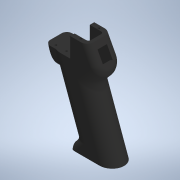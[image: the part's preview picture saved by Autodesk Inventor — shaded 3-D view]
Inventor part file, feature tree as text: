
AUTODESK INVENTOR PART (.ipt)
format: ipt  version: 2021 (Build 250183000, 183)  size: 737,280 bytes
history: native  units: mm
features: extrude x12, sketch x12, fillet x10, projected_geometry x5, plane x1, chamfer x1
ambient origin geometry x8: Origin, YZ Plane, XZ Plane, XY Plane, X Axis, Y Axis, Z Axis, Center Point
bodies: Solid1 (feature_tree)
feature tree (41):
  extrude  "Extrusion1"  TaperAngle=120.0deg  [1 undecoded]
  fillet  "Fillet10"  Radius=6.0mm
  fillet  "Fillet12"  Radius=45.0mm
  fillet  "Fillet13"  Radius=3.490659mm
  fillet  "Fillet11"  Radius=5.0mm
  extrude  "Extrusion29"  Depth=30.0mm
  extrude  "Extrusion30"  Depth=8.5mm
  plane  "Work Plane2"
  extrude  "Extrusion40"  Depth=20.0mm
  extrude  "Extrusion41"  Depth=33.0mm TaperAngle=0.0deg
  extrude  "Extrusion32"  Depth=12.0mm
  extrude  "Extrusion39"  Depth=10.0mm
  extrude  "Extrusion42"  Depth=20.0mm
  fillet  "Fillet15"  Radius=14.0mm
  fillet  "Fillet17"  Radius=11.2mm
  fillet  "Fillet18"  Radius=20.0mm
  extrude  "Extrusion44"  Depth=10.0mm
  fillet  "Fillet19"  Radius=10.0mm
  chamfer  "Chamfer6"  Distance=14.0mm
  fillet  "Fillet20"  Radius=16.0mm
  extrude  "Extrusion46"  Depth=10.0mm
  fillet  "Fillet21"  Radius=16.0mm
  extrude  "Extrusion45"  Depth=10.0mm
  extrude  "Extrusion47"  Depth=10.0mm
  sketch  "Sketch1"  dims[d1=100.0mm d2=120.0deg d3=6.0mm d5=45.0mm d6=3.490659mm d8=5.0mm]
  sketch  "Sketch29"  dims[d12=32.0mm d13=0.0mm d193=30.0mm]
  sketch  "Sketch30"  dims[d199=16.0mm d200=8.5mm]
  sketch  "Sketch31"  dims[d201=35.0mm d202=20.0mm]
  sketch  "Sketch32"  dims[d203=15.0mm d204=33.0mm d205=0.0mm]
  sketch  "Sketch39"  dims[d208=24.0mm d209=12.0mm]
  projected_geometry  "Projected Loop40"
  projected_geometry  "Projected Loop41"
  sketch  "Sketch40"  dims[d210=10.0mm d211=2.8mm]
  projected_geometry  "Projected Loop42"
  sketch  "Sketch41"  dims[d212=15.0mm d213=0.0mm d214=20.0mm d217=14.0mm d218=11.2mm d219=20.0mm]
  projected_geometry  "Projected Loop43"
  sketch  "Sketch43"  dims[d220=10.0mm d221=2.8mm d222=10.0mm d223=0.0mm]
  sketch  "Sketch44"  dims[d260=12.5mm]
  sketch  "Sketch45"  dims[d261=16.5mm]
  projected_geometry  "Projected Loop45"
  sketch  "Sketch46"  dims[d262=8.0mm d263=14.0mm d264=0.0mm d266=16.0mm d267=16.0mm d268=16.0mm d269=14.0mm d270=26.0mm d271=17.0mm d272=22.0mm d275=22.75mm d276=80.0mm d277=0.0mm d278=0.0mm d279=5.0mm d280=4.0mm d281=0.0mm d282=4.0mm d283=11.0mm d285=105.0deg d286=20.0mm d287=0.0mm d289=5.25mm d290=0.0mm d294=5.0mm d296=3.0mm d297=15.0mm d298=20.0mm d299=10.0mm d300=2.8mm d301=6.0mm d303=42.0mm d304=8.0mm d305=0.0mm d306=8.0mm d307=8.0mm d308=2.0mm d309=45.0deg d310=3.0mm d311=10.5mm d313=30.0mm d314=0.0mm d315=15.0mm d316=0.0mm d317=7.0mm d318=10.0mm d319=14.0mm d320=10.0mm d321=0.0mm]
note: 1 required parameter value undecoded (feature->parameter linkage not recoverable at this tier; creation-order binding heuristic only, values carry confidence <= 0.55)
